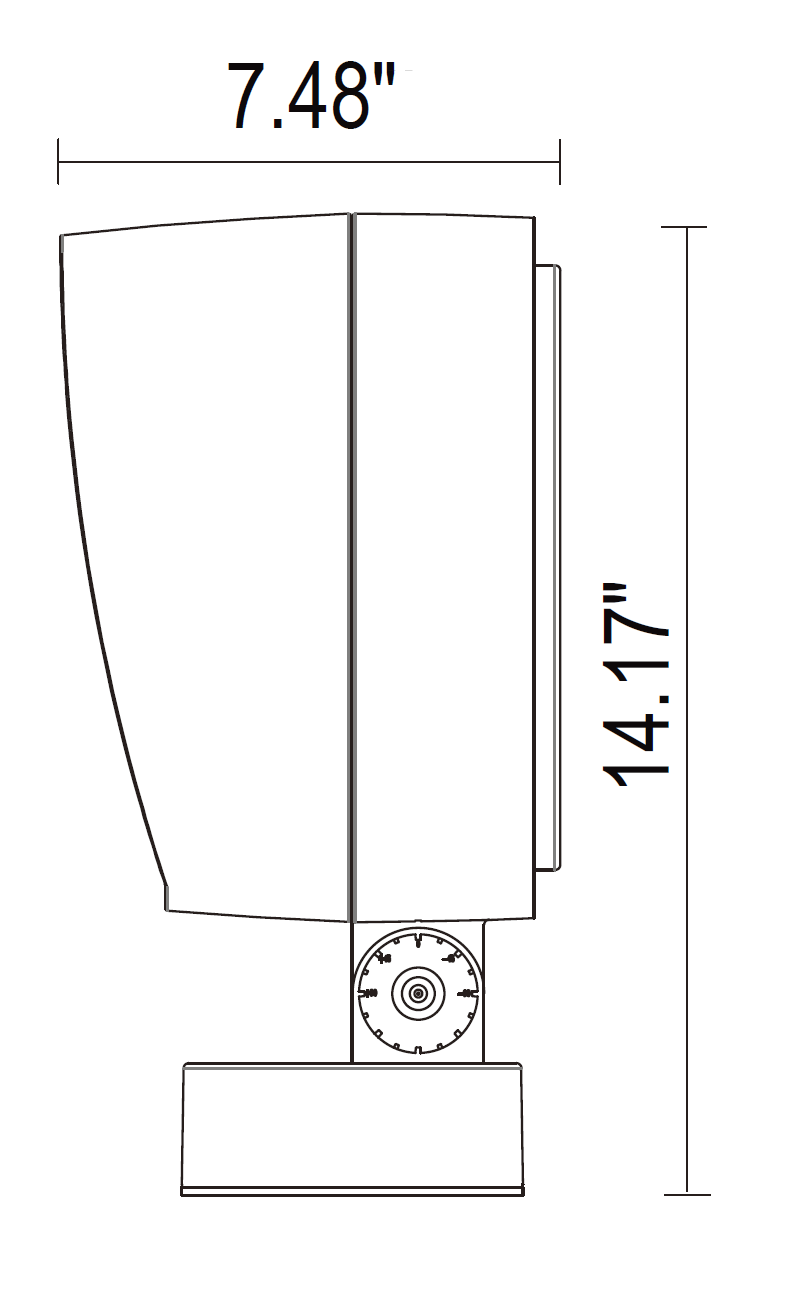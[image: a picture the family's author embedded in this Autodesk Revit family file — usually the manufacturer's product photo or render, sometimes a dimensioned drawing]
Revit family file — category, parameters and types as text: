
# Revit family: Holly Flood Light_120W_3000K
name_source: partatom
category: Lighting Fixtures
units: mm (PartAtom-declared; Revit-internal decimal feet)

## family parameters
Always vertical = Yes
Cut with Voids When Loaded = No
Light Source = No
Maintain Annotation Orientation = No
Part Type = Normal
Room Calculation Point = No
Round Connector Dimension = Use Diameter
Shared = No
Work Plane-Based = No

## types (5) — shared parameters
Assembly Code = HOLLY Flood Light - Canopy Cover
CCT = 3000K
CRI = 80
Default Elevation = 0' - 0"
Height = 1' - 2 3/16"
IP Rating = 65
Input Voltage = 120-277V
Lamp = LED
Load Classification = Lighting
Manufacturer = Above All Lighting
Power Factor = 0.9
URL = https://www.abovealllighting.com
Wattage Comments = 120W

## per-type parameters (varying)
| type | Beam Angle | Delivered Lumen | Light Source | Model | Width |
| Holly Flood _120w_3000K_5° | 5.00° | 6000 lx | 120W-Tiltable : Holly Flood _120w_3000K_5° | HOFL_C120301_5 | 10' - 7 9/16" |
| Holly Flood _120w_3000K_15° | 15.00° | 10000 lx | 120W-Tiltable : Holly Flood _120w_3000K_15° | HOFL_C120301_15 | 0' - 10 5/8" |
| Holly Flood _120w_3000K_24° | 24.00° | 10000 lx | 120W-Tiltable : Holly Flood _120w_3000K_24° | HOFL_C120301_24 | 0' - 10 5/8" |
| Holly Flood _120w_3000K_36° | 36.00° | 10000 lx | 120W-Tiltable : Holly Flood _120w_3000K_36° | HOFL_C120301_36 | 0' - 10 5/8" |
| Holly Flood _120w_3000K_50° | 50.00° | 10000 lx | 120W-Tiltable : Holly Flood _120w_3000K_50° | HOFL_C120301_50 | 0' - 10 5/8" |

## geometry (parser evidence)
native form markers: Sweep x7
no freeform markers — native parametric forms only
